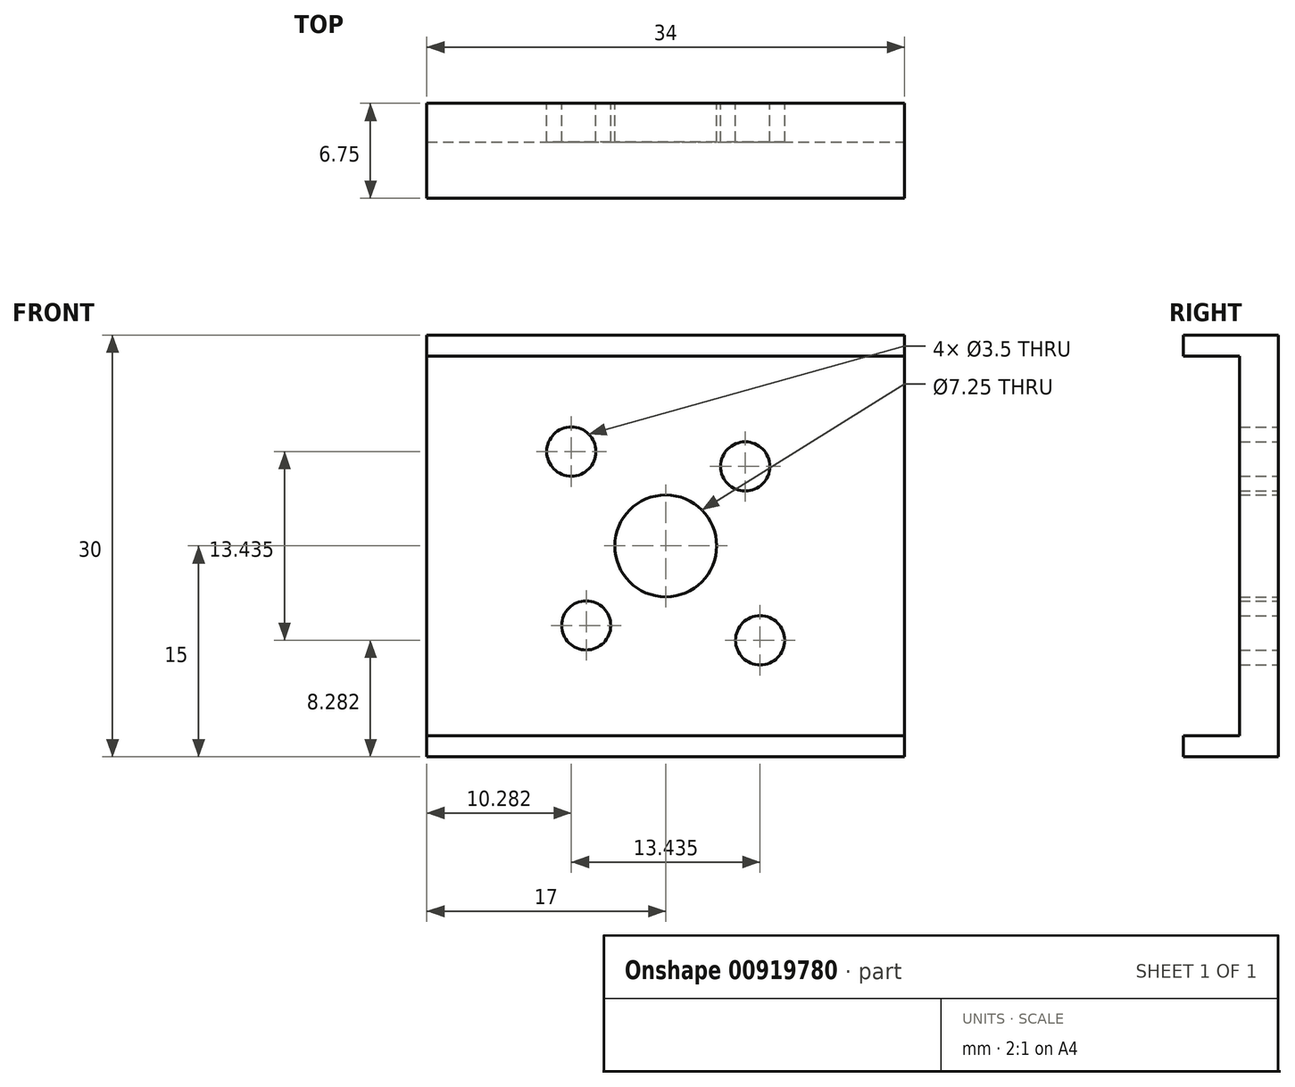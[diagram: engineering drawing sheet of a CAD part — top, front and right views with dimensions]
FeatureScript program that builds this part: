
annotation { "Feature Type Name" : "Feature", "Feature Type Description" : "" }
export const myFeature = defineFeature(function(context is Context, id is Id, definition is map)
    precondition{}
    {
        {
            var Q0;
            Q0=qCreatedBy(makeId("Front.planeOp"),FACE);
            var sketch = newSketch(context, id + "F0", { "sketchPlane" : qUnion([Q0])});
            skLineSegment(sketch, "E0.bottom", {"start": v(17, 15) * mm, "end": v(-17, 15) * mm});
            skLineSegment(sketch, "E0.top", {"start": v(17, -15) * mm, "end": v(-17, -15) * mm});
            skLineSegment(sketch, "E0.left", {"start": v(17, 15) * mm, "end": v(17, -15) * mm});
            skLineSegment(sketch, "E0.right", {"start": v(-17, 15) * mm, "end": v(-17, -15) * mm});
            skPoint(sketch, "E0.middle", {"position": v(0, 0) * mm});
            skLineSegment(sketch, "E1", {"start": v(0, 0) * mm, "end": v(-6.72, 6.72) * mm, "construction": true});
            skLineSegment(sketch, "E2", {"start": v(0, 0) * mm, "end": v(-7.4, 0) * mm, "construction": true});
            skLineSegment(sketch, "E3", {"start": v(0, 0) * mm, "end": v(5.66, 5.66) * mm, "construction": true});
            skLineSegment(sketch, "E4", {"start": v(0, 0) * mm, "end": v(-5.66, -5.66) * mm, "construction": true});
            skLineSegment(sketch, "E5", {"start": v(0, 0) * mm, "end": v(6.72, -6.72) * mm, "construction": true});
            skCircle(sketch, "E6", {"center": v(5.66, 5.66) * mm, "radius": 1.75 * mm});
            skCircle(sketch, "E7", {"center": v(-5.66, -5.66) * mm, "radius": 1.75 * mm});
            skCircle(sketch, "E8", {"center": v(6.72, -6.72) * mm, "radius": 1.75 * mm});
            skCircle(sketch, "E9", {"center": v(-6.72, 6.72) * mm, "radius": 1.75 * mm});
            skCircle(sketch, "E10", {"center": v(0, 0) * mm, "radius": 3.62 * mm});
            skSolve(sketch);
        }
        {
            var Q0;
            Q0=makeQuery(id+"F0.imprint","IMPRINT",FACE,{"disambiguationData":[TD([[makeQuery(id+"F0.imprint","IMPRINT",EDGE,{"derivedFrom":sQuery(id+"F0.wireOp",EDGE,"E0.right")}),-1.0]])]});
            var Q1;
            Q1=makeQuery(id+"F0.imprint","IMPRINT",FACE,{"disambiguationData":[TD([[makeQuery(id+"F0.imprint","IMPRINT",EDGE,{"derivedFrom":sQuery(id+"F0.wireOp",EDGE,"E0.top")}),1.0]])]});
            var Q2;
            Q2=makeQuery(id+"F0.imprint","IMPRINT",FACE,{"disambiguationData":[TD([[makeQuery(id+"F0.imprint","IMPRINT",EDGE,{"derivedFrom":sQuery(id+"F0.wireOp",EDGE,"E0.left")}),1.0]])]});
            var Q3;
            Q3=makeQuery(id+"F0.imprint","IMPRINT",FACE,{"disambiguationData":[TD([[makeQuery(id+"F0.imprint","IMPRINT",EDGE,{"derivedFrom":sQuery(id+"F0.wireOp",EDGE,"E0.bottom")}),1.0]])]});
            extrude(context, id + "F1", {"entities" : qUnion([Q0, Q1, Q2, Q3]), "depth" : 2.75 * mm, "offsetDistance" : 25 * mm});
        }
        {
            var Q0;
            Q0=makeQuery(id+"F1.opExtrude","CAP_FACE",FACE,{"disambiguationData":[OSD([sQuery(id+"F0.wireOp",EDGE,"E0.bottom"),sQuery(id+"F0.wireOp",EDGE,"E0.top"),sQuery(id+"F0.wireOp",EDGE,"E0.left"),sQuery(id+"F0.wireOp",EDGE,"E0.right"),sQuery(id+"F0.wireOp",EDGE,"E6"),sQuery(id+"F0.wireOp",EDGE,"E7"),sQuery(id+"F0.wireOp",EDGE,"E8"),sQuery(id+"F0.wireOp",EDGE,"E9")])],"isStart":false});
            var sketch = newSketch(context, id + "F2", { "sketchPlane" : qUnion([Q0])});
            skLineSegment(sketch, "E11", {"start": v(-17, 15) * mm, "end": v(17, 15) * mm});
            skLineSegment(sketch, "E12", {"start": v(17, 15) * mm, "end": v(17, 13.5) * mm});
            skLineSegment(sketch, "E13", {"start": v(17, 13.5) * mm, "end": v(-17, 13.5) * mm});
            skLineSegment(sketch, "E14", {"start": v(-17, 13.5) * mm, "end": v(-17, 15) * mm});
            skLineSegment(sketch, "E15", {"start": v(17, -15) * mm, "end": v(-17, -15) * mm});
            skLineSegment(sketch, "E16", {"start": v(-17, -15) * mm, "end": v(-17, -13.5) * mm});
            skLineSegment(sketch, "E17", {"start": v(-17, -13.5) * mm, "end": v(17, -13.5) * mm});
            skLineSegment(sketch, "E18", {"start": v(17, -13.5) * mm, "end": v(17, -15) * mm});
            skSolve(sketch);
        }
        {
            var Q0;
            Q0=makeQuery(id+"F2.imprint","IMPRINT",FACE,{"disambiguationData":[TD([[makeQuery(id+"F2.imprint","IMPRINT",EDGE,{"derivedFrom":sQuery(id+"F2.wireOp",EDGE,"E11")}),1.0]])]});
            var Q1;
            Q1=makeQuery(id+"F2.imprint","IMPRINT",FACE,{"disambiguationData":[TD([[makeQuery(id+"F2.imprint","IMPRINT",EDGE,{"derivedFrom":sQuery(id+"F2.wireOp",EDGE,"E15")}),-1.0]])]});
            extrude(context, id + "F3", {"entities" : qUnion([Q0, Q1]), "operationType" : NewBodyOperationType.ADD, "depth" : 4 * mm, "offsetDistance" : 25 * mm});
        }
    });
